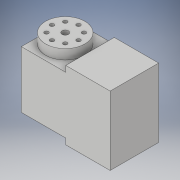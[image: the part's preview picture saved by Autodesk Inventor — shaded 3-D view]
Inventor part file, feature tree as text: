
AUTODESK INVENTOR PART (.ipt)
format: ipt  version: 2019 (Build 230136000, 136)  size: 163,840 bytes
history: native  units: mm
features: sketch x8, extrude x5, hole x3
ambient origin geometry x8: Origin, YZ Plane, XZ Plane, XY Plane, X Axis, Y Axis, Z Axis, Center Point
bodies: Solid1 (feature_tree)
feature tree (16):
  extrude  "Extrusion1"  Depth=24.7mm
  extrude  "Extrusion2"  Depth=10.0mm
  hole  "Hole1"  [1 undecoded]
  hole  "Hole2"  [1 undecoded]
  extrude  "Extrusion3"  Depth=10.0mm
  hole  "Hole3"  [1 undecoded]
  extrude  "Extrusion4"  Depth=3.0mm TaperAngle=0.0deg
  extrude  "Extrusion5"  Depth=3.0mm TaperAngle=0.0deg
  sketch  "Sketch1"  dims[d0=45.2mm d1=24.7mm]
  sketch  "Sketch2"  dims[d2=29.0mm d3=0.0mm d4=10.0mm]
  sketch  "Sketch3"  dims[d5=20.0mm d6=5.0mm d7=0.0mm]
  sketch  "Sketch4"  dims[d8=13.5mm d9=80.0mm d11=360.0deg]
  sketch  "Sketch5"  dims[d13=2.0mm d14=6.0mm d15=6.0mm d16=8.5mm d17=90.0deg d18=8.0mm d19=20.594885mm]
  sketch  "Sketch6"  dims[d20=3.25mm d21=6.0mm d22=6.0mm d23=8.5mm d24=90.0deg d25=8.0mm d26=20.594885mm d27=10.0mm]
  sketch  "Sketch7"  dims[d28=6.0mm d29=4.0mm d30=0.0mm]
  sketch  "Sketch8"  dims[d31=2.75mm d32=6.0mm d33=6.0mm d34=8.5mm d35=90.0deg d36=8.0mm d37=20.594885mm d38=3.0mm d39=0.0mm d40=3.0mm d41=0.0mm]
note: 3 required parameter values undecoded (feature->parameter linkage not recoverable at this tier; creation-order binding heuristic only, values carry confidence <= 0.55)
